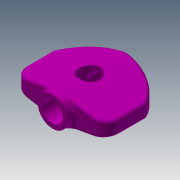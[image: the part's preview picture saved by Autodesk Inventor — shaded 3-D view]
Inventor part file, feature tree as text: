
AUTODESK INVENTOR PART (.ipt)
format: ipt  version: 2014 (Build 180170000, 170)  size: 290,304 bytes
history: native  units: mm (DEFAULTED — no unit token found)
features: sketch x4, extrude x4, fillet x3, plane x1
ambient origin geometry x8: Origin, YZ Plane, XZ Plane, XY Plane, X Axis, Y Axis, Z Axis, Center Point
bodies: Solid1 (feature_tree)
feature tree (12):
  sketch  "Sketch1"  dims[d2=3.175mm d3=0.0mm d4=15.875mm d5=0.0mm]
  plane  "Work Plane1"
  sketch  "Sketch2"  dims[d6=3.175mm d7=0.762mm d8=15.875mm d9=0.0mm d10=0.762mm]
  extrude  "Extrusion1"  Depth=15.875mm TaperAngle=0.0deg
  extrude  "Extrusion2"  Depth=0.762mm
  fillet  "Fillet1"  Radius=15.875mm
  fillet  "Fillet2"  Radius=0.762mm
  extrude  "Extrusion3"  Depth=3.175mm
  fillet  "Fillet3"  Radius=25.4mm
  extrude  "Extrusion4"  [1 undecoded]
  sketch  "Sketch3"  dims[d12=3.175mm d13=3.175mm d14=25.4mm d15=0.0mm]
  sketch  "Sketch5"
note: 1 required parameter value undecoded (feature->parameter linkage not recoverable at this tier; creation-order binding heuristic only, values carry confidence <= 0.55)
